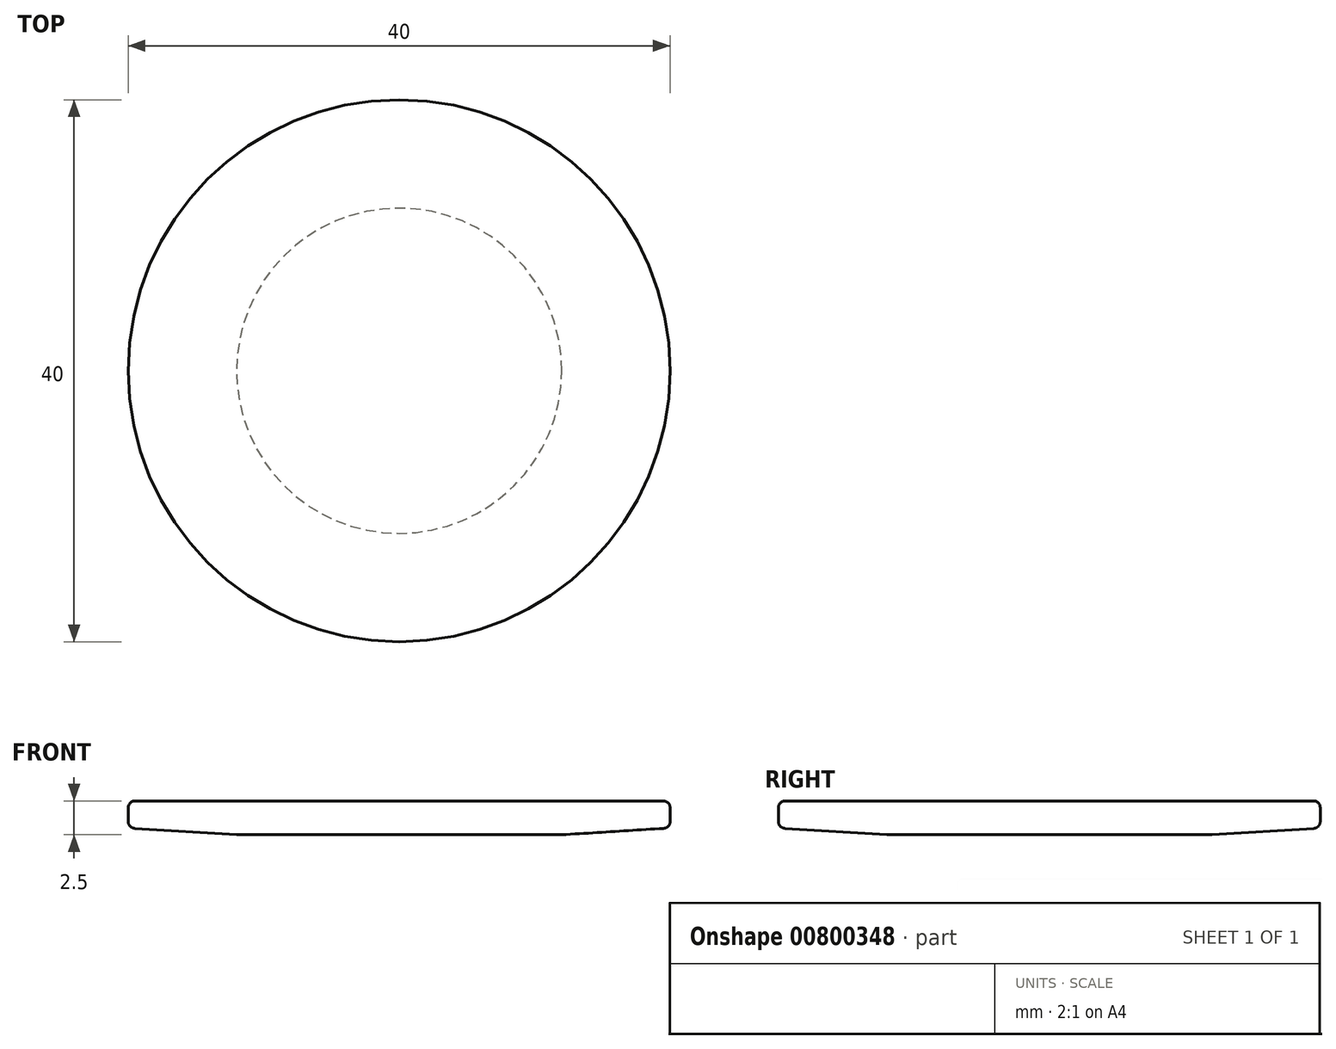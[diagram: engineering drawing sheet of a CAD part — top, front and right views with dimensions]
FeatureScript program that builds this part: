
annotation { "Feature Type Name" : "Feature", "Feature Type Description" : "" }
export const myFeature = defineFeature(function(context is Context, id is Id, definition is map)
    precondition{}
    {
        {
            var Q0;
            Q0=qCreatedBy(makeId("Front.planeOp"),FACE);
            var sketch = newSketch(context, id + "F0", { "sketchPlane" : qUnion([Q0])});
            skLineSegment(sketch, "E0", {"start": v(0, 0) * mm, "end": v(20, 0) * mm});
            skLineSegment(sketch, "E1", {"start": v(0, 0) * mm, "end": v(-20, 0) * mm});
            skLineSegment(sketch, "E2", {"start": v(0, 0) * mm, "end": v(0, -2.5) * mm});
            skLineSegment(sketch, "E3", {"start": v(0, -2.5) * mm, "end": v(-12, -2.5) * mm});
            skLineSegment(sketch, "E4", {"start": v(0, -2.5) * mm, "end": v(12, -2.5) * mm});
            skLineSegment(sketch, "E5", {"start": v(-20, 0) * mm, "end": v(-20, -2) * mm});
            skLineSegment(sketch, "E6", {"start": v(20, 0) * mm, "end": v(20, -2) * mm});
            skLineSegment(sketch, "E7", {"start": v(20, -2) * mm, "end": v(12, -2.5) * mm});
            skLineSegment(sketch, "E8", {"start": v(-12, -2.5) * mm, "end": v(-20, -2) * mm});
            skSolve(sketch);
        }
        {
            var Q0;
            Q0=makeQuery(id+"F0.imprint","IMPRINT",FACE,{"disambiguationData":[TD([[makeQuery(id+"F0.imprint","IMPRINT",EDGE,{"derivedFrom":sQuery(id+"F0.wireOp",EDGE,"E1")}),1.0]])]});
            var Q1;
            Q1=sQuery(id+"F0.wireOp",EDGE,"E2");
            revolve(context, id + "F1", {"surfaceOperationType" : NewSurfaceOperationType.NEW, "entities" : qUnion([Q0]), "axis" : qUnion([Q1]), "revolveType" : RevolveType.FULL});
        }
        {
            var Q0;
            Q0=makeQuery(id+"F1.opRevolve","SWEPT_EDGE",EDGE,{"disambiguationData":[OSD([sQuery(id+"F0.wireOp",EDGE,"E5"),sQuery(id+"F0.wireOp",EDGE,"E8")])]});
            var Q1;
            Q1=makeQuery(id+"F1.opRevolve","SWEPT_EDGE",EDGE,{"disambiguationData":[OSD([sQuery(id+"F0.wireOp",EDGE,"E1"),sQuery(id+"F0.wireOp",EDGE,"E5")])]});
            fillet(context, id + "F2", {"entities" : qUnion([Q0, Q1]), "tangentPropagation" : true, "radius" : 0.5 * mm, "defaultsChanged" : false, "vertexSettings" : [], "allowEdgeOverflow" : false});
        }
    });
